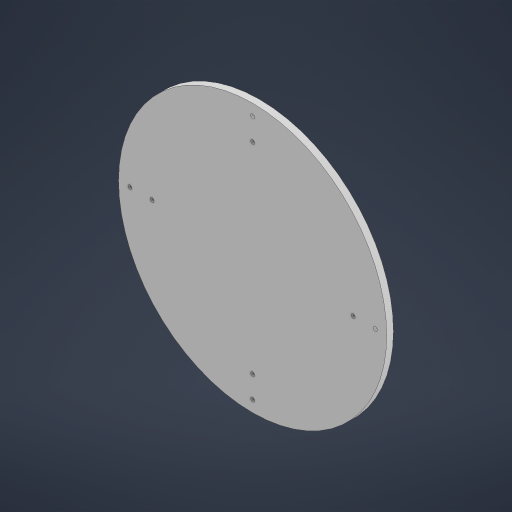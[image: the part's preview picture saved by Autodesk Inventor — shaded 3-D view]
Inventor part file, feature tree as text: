
AUTODESK INVENTOR PART (.ipt)
format: ipt  version: 2023 (Build 270158000, 158)  size: 174,592 bytes
history: native  units: mm
features: extrude x1, sketch x1
ambient origin geometry x8: Origin, YZ Plane, XZ Plane, XY Plane, X Axis, Y Axis, Z Axis, Center Point
bodies: Solid1 (feature_tree)
feature tree (2):
  extrude  "Extrusion1"  Depth=5.0mm
  sketch  "Sketch1"  dims[d0=200.0mm d2=3.0mm d3=40.0mm d5=360.0deg d7=5.0mm d8=0.0mm d10=3.0mm d11=3.0mm d12=3.0mm d13=3.0mm]
